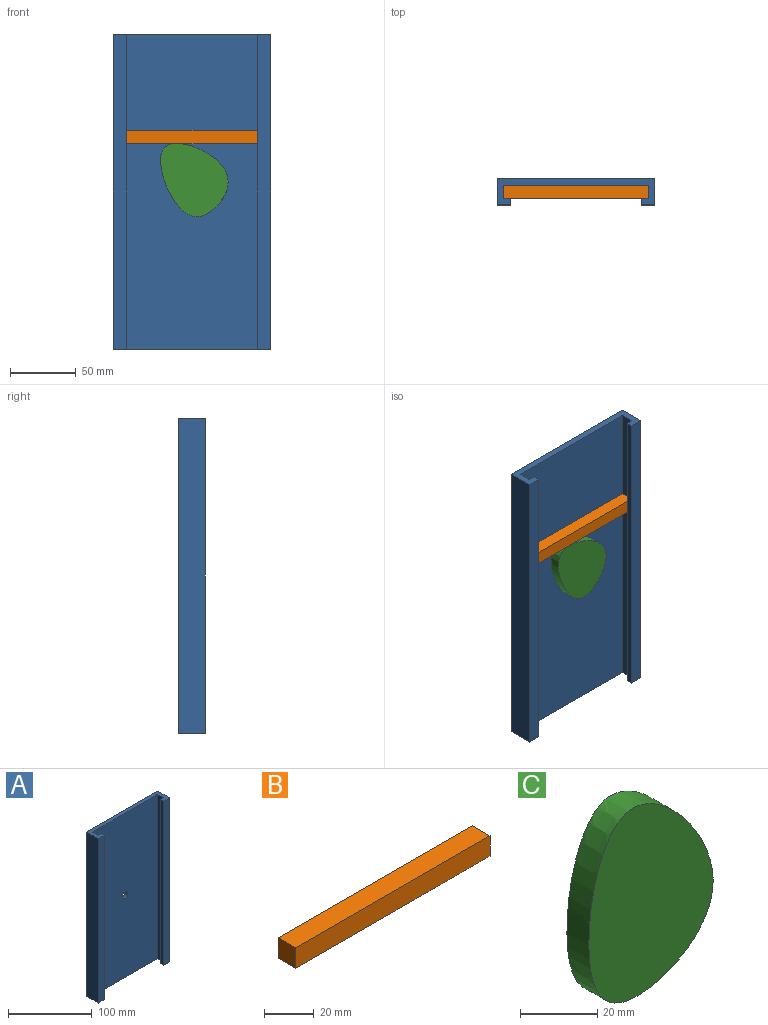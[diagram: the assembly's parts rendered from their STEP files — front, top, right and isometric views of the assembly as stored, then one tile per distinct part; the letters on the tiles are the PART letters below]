
ASSEMBLY  parts=3 mates=2
PART A: 15 faces, bbox 120x20x240 mm
  f0: plane 240x5mm, normal (1,0,0), area 1200mm2, adj f1,f3,f8,f13
  f1: plane 120x20mm, normal (0,0,-1), area 800mm2, adj f0,f2,f4,f5,f6,f7,f8,f9
  f2: plane 240x5mm, normal (-1,0,0), area 1200mm2, adj f1,f3,f6,f11
  f3: plane 120x20mm, normal (0,0,1), area 800mm2, adj f0,f2,f4,f5,f6,f7,f8,f9
  f4: plane 240x110mm, normal (0,-1,0), area 26321.5mm2, adj f1,f3,f5,f7,f14
  f5: plane 240x10mm, normal (-1,0,0), area 2400mm2, adj f1,f3,f4,f6
  f6: plane 240x5mm, normal (0,1,0), area 1200mm2, adj f1,f2,f3,f5
  f7: plane 240x10mm, normal (1,0,0), area 2400mm2, adj f1,f3,f4,f8
  f8: plane 240x5mm, normal (0,1,0), area 1200mm2, adj f0,f1,f3,f7
  f9: plane 240x120mm, normal (0,1,0), area 28721.5mm2, adj f1,f3,f10,f12,f14
  f10: plane 240x20mm, normal (1,0,0), area 4800mm2, adj f1,f3,f9,f11
  f11: plane 240x10mm, normal (0,-1,0), area 2400mm2, adj f1,f2,f3,f10
  f12: plane 240x20mm, normal (-1,0,0), area 4800mm2, adj f1,f3,f9,f13
  f13: plane 240x10mm, normal (0,-1,0), area 2400mm2, adj f0,f1,f3,f12
  f14: cylinder r=5mm len=10mm, axis (0,-1,0), area 157.1mm2, adj f4,f9
PART B: 6 faces, bbox 110x10x10 mm
  f0: plane 10x10mm, normal (1,0,0), area 100mm2, adj f1,f2,f4,f5
  f1: plane 110x10mm, normal (0,0,1), area 1100mm2, adj f0,f3,f4,f5
  f2: plane 110x10mm, normal (0,0,-1), area 1100mm2, adj f0,f3,f4,f5
  f3: plane 10x10mm, normal (-1,0,0), area 100mm2, adj f1,f2,f4,f5
  f4: plane 110x10mm, normal (0,1,0), area 1100mm2, adj f0,f1,f2,f3
  f5: plane 110x10mm, normal (0,-1,0), area 1100mm2, adj f0,f1,f2,f3
PART C: 5 faces, bbox 50.3x15x63.8 mm
  f0: plane 10x10mm, normal (0,1,0), area 78.5mm2, adj f1
  f1: cylinder r=5mm len=10mm, axis (0,-1,0), area 219.9mm2, adj f0,f4
  f2: extruded ~60.06x45.27mm, area 1333.7mm2, adj f3,f4
  f3: plane 63.76x50.28mm, normal (0,-1,0), area 2088.4mm2, adj f2
  f4: plane 63.76x50.28mm, normal (0,1,0), area 2009.9mm2, adj f1,f2
PLACE A at identity fixed
PLACE B t=(0,0,-73.05)mm
PLACE C rot(axis=(0,-1,0),29.3deg) t=(-104.69,0,-58.65)mm
MATE revolute A.f14 <-> C.f1  axis (0,1,0) through (0,7,0)mm
MATE slider A.f3 <-> B.f1  axis (0,0,1) through (-55,2,120)mm
